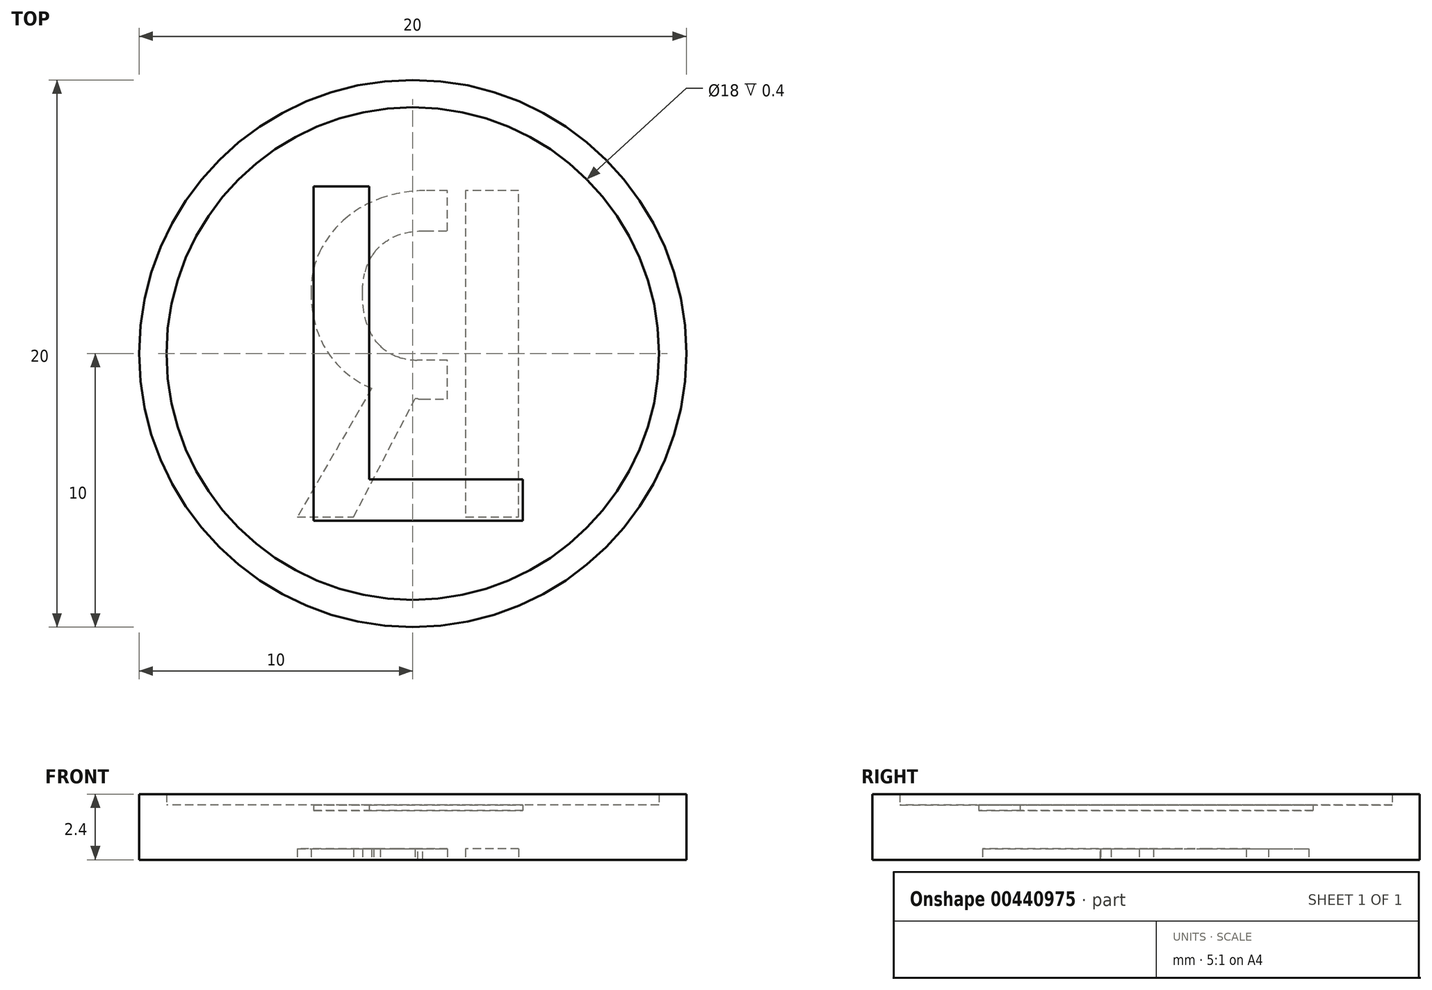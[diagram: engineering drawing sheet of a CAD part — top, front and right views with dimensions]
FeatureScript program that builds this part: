
annotation { "Feature Type Name" : "Feature", "Feature Type Description" : "" }
export const myFeature = defineFeature(function(context is Context, id is Id, definition is map)
    precondition{}
    {
        {
            var Q0;
            Q0=qCreatedBy(makeId("Top.planeOp"),FACE);
            var sketch = newSketch(context, id + "F0", { "sketchPlane" : qUnion([Q0])});
            skCircle(sketch, "E0", {"center": v(0, 0) * mm, "radius": 10 * mm});
            skText(sketch, "E1", { "text": "L", "fontName": "AllertaStencil-Regular.ttf"});
            const initialGuessF0  = {"E1": [-0.00516, -0.00611, 1, 0, 0.01222]};
            skSetInitialGuess(sketch, initialGuessF0);
            skSolve(sketch);
        }
        {
            var Q0;
            Q0=qSketchRegion(id+"F0",true);
            extrude(context, id + "F1", {"entities" : qUnion([Q0]), "depth" : 2 * mm});
        }
        {
            var Q0;
            Q0=makeQuery(id+"F0.imprint","IMPRINT",FACE,{"disambiguationData":[TD([[makeQuery(id+"F0.imprint","IMPRINT",EDGE,{"derivedFrom":sQuery(id+"F0.wireOp",EDGE,"E1.sketch_text.stroke-0")}),-1.0]])]});
            extrude(context, id + "F2", {"entities" : qUnion([Q0]), "operationType" : NewBodyOperationType.ADD, "depth" : 1.8 * mm});
        }
        {
            var Q0;
            Q0=makeQuery(id+"F1.opExtrude","CAP_FACE",FACE,{"disambiguationData":[OSD([sQuery(id+"F0.wireOp",EDGE,"E0"),sQuery(id+"F0.wireOp",EDGE,"E1.sketch_text.stroke-0"),sQuery(id+"F0.wireOp",EDGE,"E1.sketch_text.stroke-1"),sQuery(id+"F0.wireOp",EDGE,"E1.sketch_text.stroke-2"),sQuery(id+"F0.wireOp",EDGE,"E1.sketch_text.stroke-3"),sQuery(id+"F0.wireOp",EDGE,"E1.sketch_text.stroke-4"),sQuery(id+"F0.wireOp",EDGE,"E1.sketch_text.stroke-5")])],"isStart":false});
            var sketch = newSketch(context, id + "F3", { "sketchPlane" : qUnion([Q0])});
            skCircle(sketch, "E2.0.0", {"center": v(0, 0) * mm, "radius": 10 * mm});
            skCircle(sketch, "E3.0", {"center": v(0, 0) * mm, "radius": 9 * mm});
            skSolve(sketch);
        }
        {
            var Q0;
            Q0=makeQuery(id+"F3.imprint","IMPRINT",FACE,{"disambiguationData":[TD([[makeQuery(id+"F3.imprint","IMPRINT",EDGE,{"derivedFrom":sQuery(id+"F3.wireOp",EDGE,"E2.0.0")}),1.0]])]});
            extrude(context, id + "F4", {"entities" : qUnion([Q0]), "operationType" : NewBodyOperationType.ADD, "depth" : .4 * mm});
        }
        {
            var Q0;
            {var subQ0=sQuery(id+"F0.wireOp",EDGE,"E1.sketch_text.stroke-5");var subQ1=sQuery(id+"F0.wireOp",EDGE,"E1.sketch_text.stroke-4");var subQ2=sQuery(id+"F0.wireOp",EDGE,"E1.sketch_text.stroke-3");var subQ3=sQuery(id+"F0.wireOp",EDGE,"E1.sketch_text.stroke-2");var subQ4=sQuery(id+"F0.wireOp",EDGE,"E1.sketch_text.stroke-1");var subQ5=sQuery(id+"F0.wireOp",EDGE,"E1.sketch_text.stroke-0");Q0=makeQuery(id+"F2.boolean.opBoolean","MERGE",FACE,{"derivedFrom":[makeQuery(id+"F1.opExtrude","CAP_FACE",FACE,{"disambiguationData":[OSD([sQuery(id+"F0.wireOp",EDGE,"E0"),subQ5,subQ4,subQ3,subQ2,subQ1,subQ0])],"isStart":true}),makeQuery(id+"F2.opExtrude","CAP_FACE",FACE,{"disambiguationData":[OSD([subQ5,subQ4,subQ3,subQ2,subQ1,subQ0])],"isStart":true})]});}
            var sketch = newSketch(context, id + "F5", { "sketchPlane" : qUnion([Q0])});
            skCircle(sketch, "E4.0", {"center": v(0, 0) * mm, "radius": 9 * mm});
            skText(sketch, "E5", { "text": "R", "fontName": "AllertaStencil-Regular.ttf"});
            const initialGuessF5  = {"E5": [0.00533, 0.00597, -1, 0, 0.01193]};
            skSetInitialGuess(sketch, initialGuessF5);
            skSolve(sketch);
        }
        {
            var Q0;
            Q0=makeQuery(id+"F5.imprint","IMPRINT",FACE,{"disambiguationData":[TD([[makeQuery(id+"F5.imprint","IMPRINT",EDGE,{"derivedFrom":sQuery(id+"F5.wireOp",EDGE,"E5.sketch_text.stroke-0")}),-1.0]])]});
            var Q1;
            Q1=makeQuery(id+"F5.imprint","IMPRINT",FACE,{"disambiguationData":[TD([[makeQuery(id+"F5.imprint","IMPRINT",EDGE,{"derivedFrom":sQuery(id+"F5.wireOp",EDGE,"E5.sketch_text.stroke-4")}),-1.0]])]});
            extrude(context, id + "F6", {"entities" : qUnion([Q0, Q1]), "operationType" : NewBodyOperationType.REMOVE, "oppositeDirection" : true, "depth" : .4 * mm});
        }
        {
            var Q0;
            Q0=makeQuery(id+"F2.opExtrude","CAP_FACE",FACE,{"disambiguationData":[OSD([sQuery(id+"F0.wireOp",EDGE,"E1.sketch_text.stroke-0"),sQuery(id+"F0.wireOp",EDGE,"E1.sketch_text.stroke-1"),sQuery(id+"F0.wireOp",EDGE,"E1.sketch_text.stroke-2"),sQuery(id+"F0.wireOp",EDGE,"E1.sketch_text.stroke-3"),sQuery(id+"F0.wireOp",EDGE,"E1.sketch_text.stroke-4"),sQuery(id+"F0.wireOp",EDGE,"E1.sketch_text.stroke-5")])],"isStart":false});
            extrude(context, id + "F7", {"entities" : qUnion([Q0]), "depth" : .2 * mm});
        }
    });
